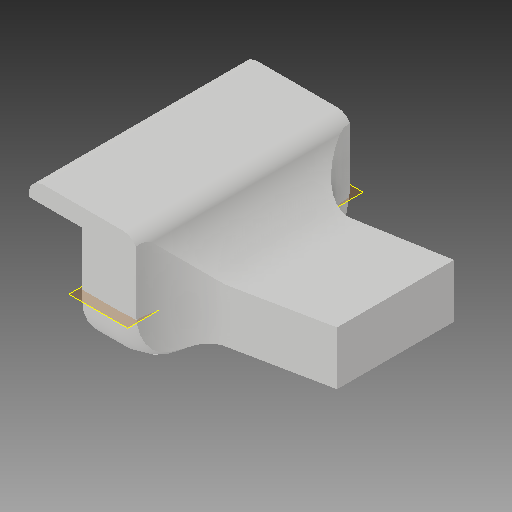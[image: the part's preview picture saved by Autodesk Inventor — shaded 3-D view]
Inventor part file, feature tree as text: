
AUTODESK INVENTOR PART (.ipt)
format: ipt  version: 2018 (Build 220112000, 112)  size: 229,376 bytes
history: native  units: in
note: dims shown in document units (in); Inventor stores cm internally (conversion verified against a paired STEP export)
features: extrude x9, sketch x9, fillet x7, other x2, plane x1, reference x1
ambient origin geometry x8: Origin, YZ Plane, XZ Plane, XY Plane, X Axis, Y Axis, Z Axis, Center Point
bodies: Solid1 (feature_tree)
feature tree (29):
  extrude  "Extrusion1"  Depth=0.6in
  plane  "Work Plane1"
  extrude  "Extrusion2"  Depth=0.15in
  extrude  "Extrusion4"  Depth=0.15in TaperAngle=0.0deg
  extrude  "Extrusion5"  Depth=0.15in TaperAngle=0.0deg
  extrude  "Extrusion6"  Depth=0.3in
  extrude  "Extrusion7"  Depth=0.05in TaperAngle=0.0deg
  extrude  "Extrusion8"  Depth=0.125in
  extrude  "Extrusion10"  Depth=0.125in
  fillet  "Fillet4"  Radius=0.125in
  fillet  "Fillet5"  Radius=0.0394in
  fillet  "Fillet6"  Radius=0.125in
  fillet  "Fillet7"  Radius=1.0in
  fillet  "Fillet8"  [1 undecoded]
  fillet  "Fillet9"  [1 undecoded]
  fillet  "Fillet10"  [1 undecoded]
  extrude  "Extrusion11"  [1 undecoded]
  sketch  "Sketch1"  dims[d0=0.3in d1=0.6in]
  sketch  "Sketch2"  dims[d2=0.15in d3=0.0in d4=2.0in]
  sketch  "Sketch4"  dims[d5=0.15in d6=0.0in d9=0.15in d10=0.0in]
  sketch  "Sketch5"  dims[d11=0.15in d12=0.0in d13=0.15in d14=0.0in]
  sketch  "Sketch6"  dims[d15=0.15in d16=0.0in d18=0.3in]
  sketch  "Sketch7"  dims[d19=0.05in d20=0.0in d27=0.05in d28=0.0in]
  sketch  "Sketch8"  dims[d29=0.125in d30=0.125in]
  sketch  "Sketch11"  dims[d31=0.125in d32=0.125in d33=0.125in d34=0.0394in d35=0.125in d36=1.0in d37=0.0in]
  sketch  "Sketch12"
  reference  "Reference1"
  other  "ArmTruss.iam"
  other  "bottomARM:1"
note: 4 required parameter values undecoded (feature->parameter linkage not recoverable at this tier; creation-order binding heuristic only, values carry confidence <= 0.55)
